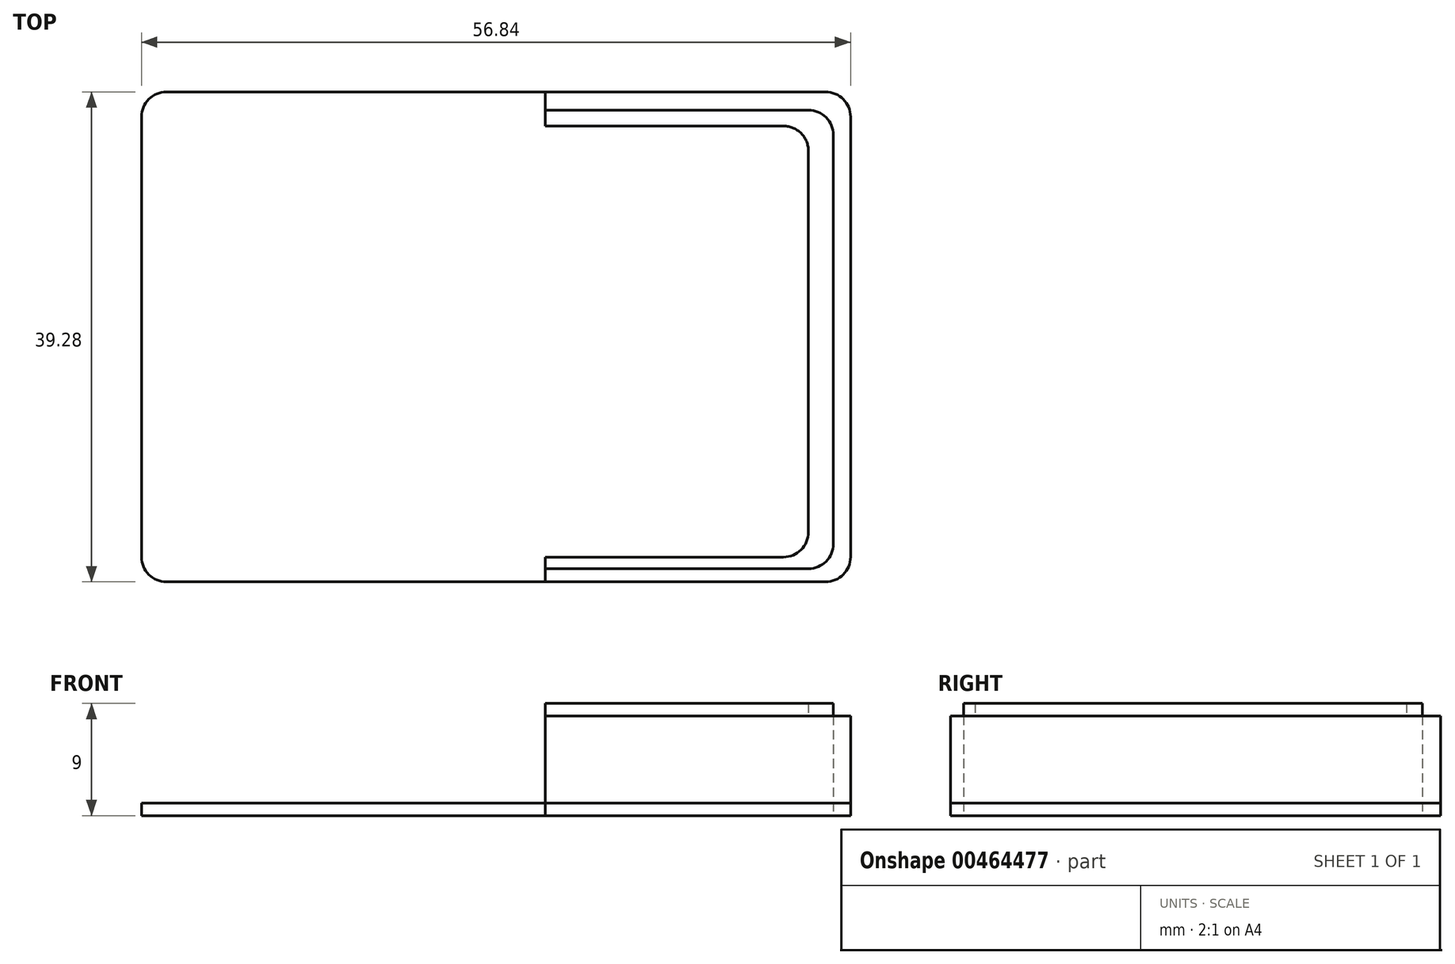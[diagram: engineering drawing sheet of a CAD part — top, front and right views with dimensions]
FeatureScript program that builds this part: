
annotation { "Feature Type Name" : "Feature", "Feature Type Description" : "" }
export const myFeature = defineFeature(function(context is Context, id is Id, definition is map)
    precondition{}
    {
        {
            var Q0;
            Q0=qCreatedBy(makeId("Top.planeOp"),FACE);
            var sketch = newSketch(context, id + "F0", { "sketchPlane" : qUnion([Q0])});
            skLineSegment(sketch, "E0.bottom", {"start": v(-30.36, 19.23) * mm, "end": v(22.48, 19.23) * mm});
            skLineSegment(sketch, "E0.top", {"start": v(-30.36, -20.05) * mm, "end": v(22.48, -20.05) * mm});
            skLineSegment(sketch, "E0.left", {"start": v(-32.36, 17.23) * mm, "end": v(-32.36, -18.05) * mm});
            skLineSegment(sketch, "E0.right", {"start": v(24.48, 17.23) * mm, "end": v(24.48, -18.05) * mm});
            skPoint(sketch, "E1.visualSharp", {"position": v(-32.36, 19.23) * mm});
            skArc(sketch, "E1.filletArc", {"start": v(-30.36, 19.23) * mm, "mid": v(-31.77, 18.65) * mm, "end": v(-32.36, 17.23) * mm});
            skPoint(sketch, "E2.visualSharp", {"position": v(24.48, 19.23) * mm});
            skArc(sketch, "E2.filletArc", {"start": v(24.48, 17.23) * mm, "mid": v(23.9, 18.65) * mm, "end": v(22.48, 19.23) * mm});
            skPoint(sketch, "E3.visualSharp", {"position": v(24.48, -20.05) * mm});
            skArc(sketch, "E3.filletArc", {"start": v(22.48, -20.05) * mm, "mid": v(23.9, -19.47) * mm, "end": v(24.48, -18.05) * mm});
            skPoint(sketch, "E4.visualSharp", {"position": v(-32.36, -20.05) * mm});
            skArc(sketch, "E4.filletArc", {"start": v(-32.36, -18.05) * mm, "mid": v(-31.77, -19.47) * mm, "end": v(-30.36, -20.05) * mm});
            skSolve(sketch);
        }
        {
            var Q0;
            Q0=makeQuery(id+"F0.imprint","IMPRINT",FACE,{"disambiguationData":[TD([[makeQuery(id+"F0.imprint","IMPRINT",EDGE,{"derivedFrom":sQuery(id+"F0.wireOp",EDGE,"E0.bottom")}),-1.0]])]});
            extrude(context, id + "F1", {"entities" : qUnion([Q0]), "depth" : 1 * mm});
        }
        {
            var Q0;
            Q0=makeQuery(id+"F0.imprint","IMPRINT",FACE,{"disambiguationData":[TD([[makeQuery(id+"F0.imprint","IMPRINT",EDGE,{"derivedFrom":sQuery(id+"F0.wireOp",EDGE,"E0.bottom")}),-1.0]])]});
            var sketch = newSketch(context, id + "F2", { "sketchPlane" : qUnion([Q0])});
            skLineSegment(sketch, "E5.0", {"start": v(24.48, 17.23) * mm, "end": v(24.48, -18.05) * mm});
            skArc(sketch, "E6.0", {"start": v(24.48, 17.23) * mm, "mid": v(23.9, 18.65) * mm, "end": v(22.48, 19.23) * mm});
            skArc(sketch, "E7.0", {"start": v(22.48, -20.05) * mm, "mid": v(23.9, -19.47) * mm, "end": v(24.48, -18.05) * mm});
            skLineSegment(sketch, "E8", {"start": v(22.48, 19.23) * mm, "end": v(0, 19.23) * mm});
            skLineSegment(sketch, "E9", {"start": v(22.48, -20.05) * mm, "end": v(0, -20.05) * mm});
            skLineSegment(sketch, "E10", {"start": v(0, 17.77) * mm, "end": v(21.1, 17.77) * mm});
            skLineSegment(sketch, "E11", {"start": v(23.1, 15.77) * mm, "end": v(23.1, -17) * mm});
            skLineSegment(sketch, "E12", {"start": v(21.1, -19) * mm, "end": v(0, -19) * mm});
            skLineSegment(sketch, "E13", {"start": v(0, -19) * mm, "end": v(0, -20.05) * mm});
            skLineSegment(sketch, "E14", {"start": v(0, 17.77) * mm, "end": v(0, 19.23) * mm});
            skPoint(sketch, "E15.visualSharp", {"position": v(23.1, 17.77) * mm});
            skArc(sketch, "E15.filletArc", {"start": v(23.1, 15.77) * mm, "mid": v(22.51, 17.19) * mm, "end": v(21.1, 17.77) * mm});
            skPoint(sketch, "E16.visualSharp", {"position": v(23.1, -19) * mm});
            skArc(sketch, "E16.filletArc", {"start": v(21.1, -19) * mm, "mid": v(22.51, -18.42) * mm, "end": v(23.1, -17) * mm});
            skSolve(sketch);
        }
        {
            var Q0;
            Q0 = qSketchRegion(id + "F2", true);
            extrude(context, id + "F3", {"entities" : qUnion([Q0]), "depth" : 8 * mm});
        }
        {
            var Q0;
            Q0=makeQuery(id+"F3.opExtrude","CAP_EDGE",EDGE,{"disambiguationData":[OSD([sQuery(id+"F2.wireOp",EDGE,"E11")])],"isStart":false});
            cPoint(context, id + "F4", {"entities" : qUnion([Q0]), "parameter" : 0.5});
        }
        {
            var Q0;
            Q0=qCreatedBy(makeId("Top.planeOp"),FACE);
            var Q1;
            Q1 = qCreatedBy(id + "F4" ,VERTEX);
            cPlane(context, id + "F5", {"entities" : qUnion([Q0, Q1]), "cplaneType" : CPlaneType.PLANE_POINT, "offset" : 25 * mm, "width" : 150 * mm, "height" : 150 * mm});
        }
        {
            var Q0;
            Q0=qCreatedBy(id+"F5.planeOp",FACE);
            var sketch = newSketch(context, id + "F6", { "sketchPlane" : qUnion([Q0])});
            skLineSegment(sketch, "E17.0", {"start": v(21.1, -19) * mm, "end": v(0, -19) * mm});
            skArc(sketch, "E18.0", {"start": v(21.1, -19) * mm, "mid": v(22.51, -18.42) * mm, "end": v(23.1, -17) * mm});
            skLineSegment(sketch, "E19.0", {"start": v(23.1, 15.77) * mm, "end": v(23.1, -17) * mm});
            skPoint(sketch, "E20.0", {"position": v(22.51, 17.19) * mm});
            skLineSegment(sketch, "E21.0", {"start": v(0, 17.77) * mm, "end": v(21.1, 17.77) * mm});
            skArc(sketch, "E22.0", {"start": v(23.1, 15.77) * mm, "mid": v(22.51, 17.19) * mm, "end": v(21.1, 17.77) * mm});
            skLineSegment(sketch, "E23", {"start": v(0, -19) * mm, "end": v(0, -18.07) * mm});
            skLineSegment(sketch, "E24", {"start": v(0, -18.07) * mm, "end": v(19.1, -18.07) * mm});
            skLineSegment(sketch, "E25", {"start": v(21.1, -16.07) * mm, "end": v(21.1, 14.5) * mm});
            skLineSegment(sketch, "E26", {"start": v(19.1, 16.5) * mm, "end": v(0, 16.5) * mm});
            skLineSegment(sketch, "E27", {"start": v(0, 16.5) * mm, "end": v(0, 17.77) * mm});
            skPoint(sketch, "E28.visualSharp", {"position": v(21.1, -18.07) * mm});
            skArc(sketch, "E28.filletArc", {"start": v(19.1, -18.07) * mm, "mid": v(20.5, -17.48) * mm, "end": v(21.1, -16.07) * mm});
            skPoint(sketch, "E29.visualSharp", {"position": v(21.1, 16.5) * mm});
            skArc(sketch, "E29.filletArc", {"start": v(21.1, 14.5) * mm, "mid": v(20.51, 15.91) * mm, "end": v(19.1, 16.5) * mm});
            skSolve(sketch);
        }
        {
            var Q0;
            Q0 = qSketchRegion(id + "F6", true);
            extrude(context, id + "F7", {"entities" : qUnion([Q0]), "depth" : 1 * mm});
        }
    });
